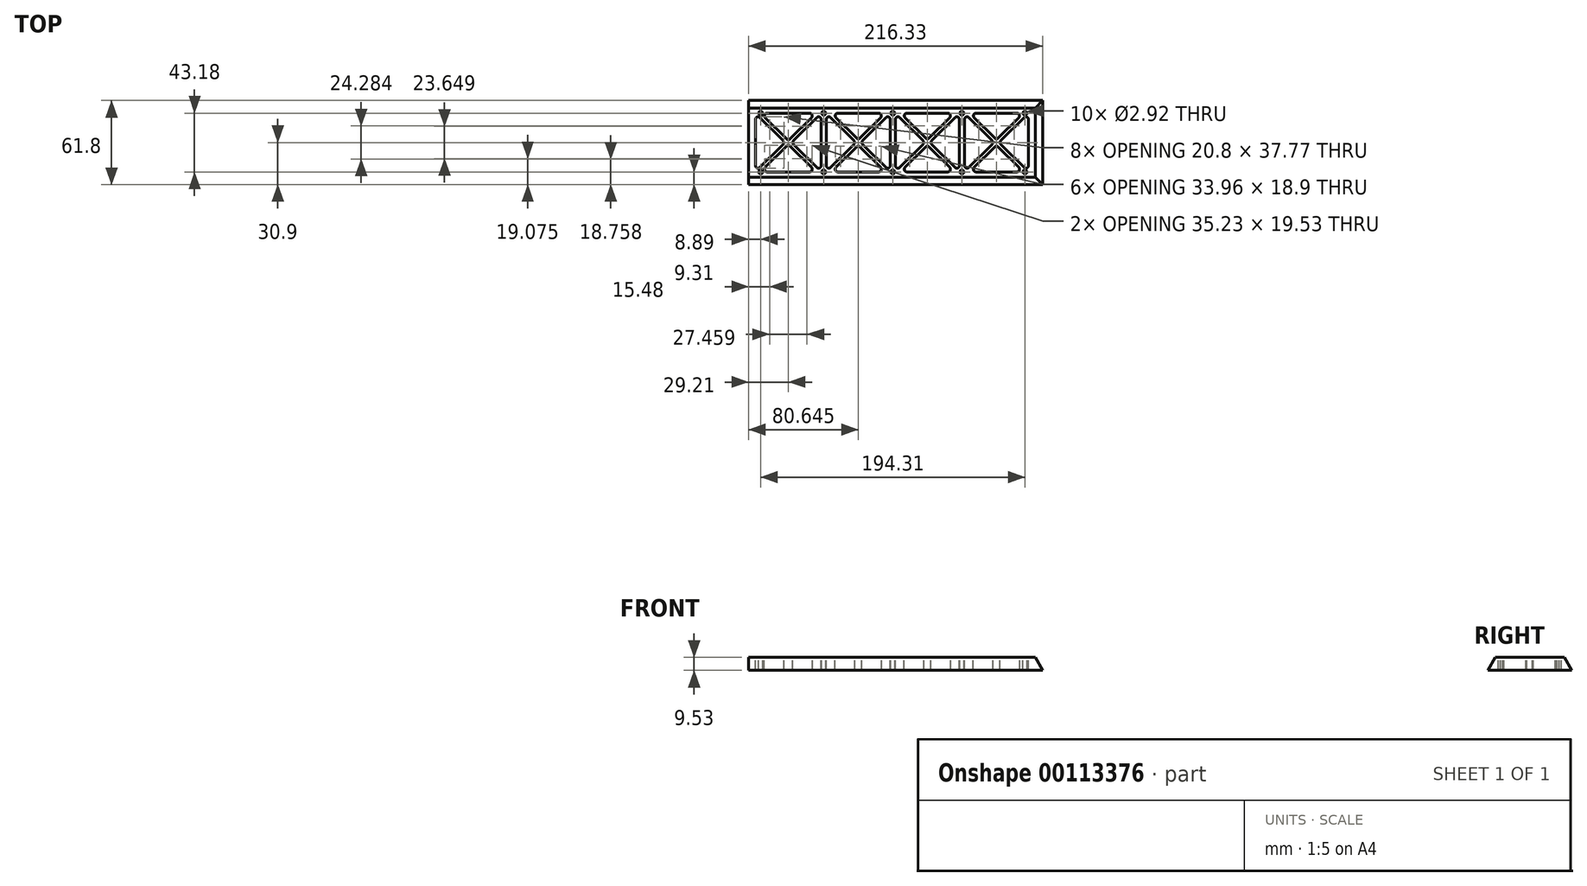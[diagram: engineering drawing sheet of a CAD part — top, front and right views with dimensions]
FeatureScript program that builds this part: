
annotation { "Feature Type Name" : "Feature", "Feature Type Description" : "" }
export const myFeature = defineFeature(function(context is Context, id is Id, definition is map)
    precondition{}
    {
        {
            var Q0;
            Q0=qCreatedBy(makeId("Top.planeOp"),FACE);
            var sketch = newSketch(context, id + "F0", { "sketchPlane" : qUnion([Q0])});
            skLineSegment(sketch, "E0.bottom", {"start": v(0, 0) * mm, "end": v(210.82, 0) * mm});
            skLineSegment(sketch, "E0.top", {"start": v(0, 50.8) * mm, "end": v(210.82, 50.8) * mm});
            skLineSegment(sketch, "E0.left", {"start": v(0, 0) * mm, "end": v(0, 50.8) * mm});
            skLineSegment(sketch, "E0.right", {"start": v(210.82, 0) * mm, "end": v(210.82, 50.8) * mm});
            skSolve(sketch);
        }
        {
            var Q0;
            Q0 = qSketchRegion(id + "F0", true);
            extrude(context, id + "F1", {"entities" : qUnion([Q0]), "depth" : 12.7 * mm, "offsetDistance" : 25.4 * mm});
        }
        {
            var Q0;
            Q0=makeQuery(id+"F1.opExtrude","CAP_FACE",FACE,{"disambiguationData":[OSD([sQuery(id+"F0.wireOp",EDGE,"E0.bottom"),sQuery(id+"F0.wireOp",EDGE,"E0.top"),sQuery(id+"F0.wireOp",EDGE,"E0.left"),sQuery(id+"F0.wireOp",EDGE,"E0.right")])],"isStart":false});
            var sketch = newSketch(context, id + "F2", { "sketchPlane" : qUnion([Q0])});
            skLineSegment(sketch, "E1", {"start": v(0, 25.4) * mm, "end": v(210.82, 25.4) * mm, "construction": true});
            skLineSegment(sketch, "E2", {"start": v(5.08, 42.4) * mm, "end": v(5.08, 8.4) * mm});
            skLineSegment(sketch, "E3", {"start": v(8.33, 7.06) * mm, "end": v(25.32, 24.05) * mm});
            skLineSegment(sketch, "E4", {"start": v(25.32, 26.75) * mm, "end": v(8.33, 43.74) * mm});
            skLineSegment(sketch, "E5", {"start": v(33.1, 26.75) * mm, "end": v(50.09, 43.74) * mm});
            skLineSegment(sketch, "E6", {"start": v(53.34, 42.4) * mm, "end": v(53.34, 8.4) * mm});
            skLineSegment(sketch, "E7", {"start": v(50.09, 7.06) * mm, "end": v(33.1, 24.05) * mm});
            skLineSegment(sketch, "E8", {"start": v(57.15, 42.4) * mm, "end": v(57.15, 8.4) * mm});
            skLineSegment(sketch, "E9", {"start": v(60.4, 7.06) * mm, "end": v(77.4, 24.05) * mm});
            skLineSegment(sketch, "E10", {"start": v(77.4, 26.75) * mm, "end": v(60.4, 43.74) * mm});
            skLineSegment(sketch, "E11", {"start": v(104.14, 42.4) * mm, "end": v(104.14, 8.4) * mm});
            skLineSegment(sketch, "E12", {"start": v(100.89, 7.06) * mm, "end": v(83.9, 24.05) * mm});
            skLineSegment(sketch, "E13", {"start": v(83.9, 26.75) * mm, "end": v(100.89, 43.74) * mm});
            skLineSegment(sketch, "E14", {"start": v(107.95, 42.4) * mm, "end": v(107.95, 8.4) * mm});
            skLineSegment(sketch, "E15", {"start": v(111.2, 7.06) * mm, "end": v(128.2, 24.05) * mm});
            skLineSegment(sketch, "E16", {"start": v(128.2, 26.75) * mm, "end": v(111.2, 43.74) * mm});
            skLineSegment(sketch, "E17", {"start": v(154.94, 42.4) * mm, "end": v(154.94, 8.4) * mm});
            skLineSegment(sketch, "E18", {"start": v(151.69, 7.06) * mm, "end": v(134.7, 24.05) * mm});
            skLineSegment(sketch, "E19", {"start": v(134.7, 26.75) * mm, "end": v(151.69, 43.74) * mm});
            skLineSegment(sketch, "E20", {"start": v(158.75, 42.4) * mm, "end": v(158.75, 8.4) * mm});
            skLineSegment(sketch, "E21", {"start": v(162, 7.06) * mm, "end": v(179, 24.05) * mm});
            skLineSegment(sketch, "E22", {"start": v(179, 26.75) * mm, "end": v(162, 43.74) * mm});
            skLineSegment(sketch, "E23", {"start": v(205.74, 42.4) * mm, "end": v(205.74, 8.4) * mm});
            skLineSegment(sketch, "E24", {"start": v(202.49, 7.06) * mm, "end": v(185.5, 24.05) * mm});
            skLineSegment(sketch, "E25", {"start": v(185.5, 26.75) * mm, "end": v(202.49, 43.74) * mm});
            skLineSegment(sketch, "E26", {"start": v(13.49, 46.99) * mm, "end": v(44.93, 46.99) * mm});
            skLineSegment(sketch, "E27", {"start": v(46.28, 43.74) * mm, "end": v(30.56, 28.02) * mm});
            skLineSegment(sketch, "E28", {"start": v(27.86, 28.02) * mm, "end": v(12.14, 43.74) * mm});
            skLineSegment(sketch, "E29", {"start": v(13.49, 3.8) * mm, "end": v(44.93, 3.8) * mm});
            skLineSegment(sketch, "E30", {"start": v(46.28, 7.06) * mm, "end": v(30.56, 22.78) * mm});
            skLineSegment(sketch, "E31", {"start": v(27.86, 22.78) * mm, "end": v(12.14, 7.06) * mm});
            skLineSegment(sketch, "E32", {"start": v(65.56, 46.99) * mm, "end": v(95.73, 46.99) * mm});
            skLineSegment(sketch, "E33", {"start": v(97.08, 43.74) * mm, "end": v(82, 28.65) * mm});
            skLineSegment(sketch, "E34", {"start": v(79.3, 28.65) * mm, "end": v(64.21, 43.74) * mm});
            skLineSegment(sketch, "E35", {"start": v(65.56, 3.8) * mm, "end": v(95.73, 3.8) * mm});
            skLineSegment(sketch, "E36", {"start": v(97.08, 7.06) * mm, "end": v(82, 22.15) * mm});
            skLineSegment(sketch, "E37", {"start": v(79.3, 22.15) * mm, "end": v(64.21, 7.06) * mm});
            skLineSegment(sketch, "E38", {"start": v(116.36, 46.99) * mm, "end": v(146.53, 46.99) * mm});
            skLineSegment(sketch, "E39", {"start": v(147.88, 43.74) * mm, "end": v(132.8, 28.65) * mm});
            skLineSegment(sketch, "E40", {"start": v(130.1, 28.65) * mm, "end": v(115.01, 43.74) * mm});
            skLineSegment(sketch, "E41", {"start": v(116.36, 3.8) * mm, "end": v(146.53, 3.8) * mm});
            skLineSegment(sketch, "E42", {"start": v(147.88, 7.06) * mm, "end": v(132.8, 22.15) * mm});
            skLineSegment(sketch, "E43", {"start": v(130.1, 22.15) * mm, "end": v(115.01, 7.06) * mm});
            skLineSegment(sketch, "E44", {"start": v(167.16, 46.99) * mm, "end": v(197.33, 46.99) * mm});
            skLineSegment(sketch, "E45", {"start": v(198.68, 43.74) * mm, "end": v(183.6, 28.65) * mm});
            skLineSegment(sketch, "E46", {"start": v(180.9, 28.65) * mm, "end": v(165.81, 43.74) * mm});
            skLineSegment(sketch, "E47", {"start": v(167.16, 3.8) * mm, "end": v(197.33, 3.8) * mm});
            skLineSegment(sketch, "E48", {"start": v(198.68, 7.06) * mm, "end": v(183.6, 22.15) * mm});
            skLineSegment(sketch, "E49", {"start": v(180.9, 22.15) * mm, "end": v(165.81, 7.06) * mm});
            skPoint(sketch, "E50.visualSharp", {"position": v(5.08, 46.99) * mm});
            skArc(sketch, "E50.filletArc", {"start": v(8.33, 43.74) * mm, "mid": v(6.26, 44.15) * mm, "end": v(5.08, 42.4) * mm});
            skPoint(sketch, "E51.visualSharp", {"position": v(5.08, 3.8) * mm});
            skArc(sketch, "E51.filletArc", {"start": v(5.08, 8.4) * mm, "mid": v(6.26, 6.65) * mm, "end": v(8.33, 7.06) * mm});
            skPoint(sketch, "E52.visualSharp", {"position": v(26.67, 25.4) * mm});
            skArc(sketch, "E52.filletArc", {"start": v(25.32, 24.05) * mm, "mid": v(25.88, 25.4) * mm, "end": v(25.32, 26.75) * mm});
            skPoint(sketch, "E53.visualSharp", {"position": v(8.89, 46.99) * mm});
            skArc(sketch, "E53.filletArc", {"start": v(13.49, 46.99) * mm, "mid": v(11.73, 45.81) * mm, "end": v(12.14, 43.74) * mm});
            skPoint(sketch, "E54.visualSharp", {"position": v(49.53, 46.99) * mm});
            skArc(sketch, "E54.filletArc", {"start": v(46.28, 43.74) * mm, "mid": v(46.7, 45.81) * mm, "end": v(44.93, 46.99) * mm});
            skPoint(sketch, "E55.visualSharp", {"position": v(29.21, 26.67) * mm});
            skArc(sketch, "E55.filletArc", {"start": v(27.86, 28.02) * mm, "mid": v(29.21, 27.46) * mm, "end": v(30.56, 28.02) * mm});
            skPoint(sketch, "E56.visualSharp", {"position": v(29.21, 24.13) * mm});
            skArc(sketch, "E56.filletArc", {"start": v(30.56, 22.78) * mm, "mid": v(29.21, 23.34) * mm, "end": v(27.86, 22.78) * mm});
            skPoint(sketch, "E57.visualSharp", {"position": v(8.9, 3.8) * mm});
            skArc(sketch, "E57.filletArc", {"start": v(12.14, 7.06) * mm, "mid": v(11.73, 4.99) * mm, "end": v(13.49, 3.8) * mm});
            skPoint(sketch, "E58.visualSharp", {"position": v(49.53, 3.8) * mm});
            skArc(sketch, "E58.filletArc", {"start": v(44.93, 3.8) * mm, "mid": v(46.7, 4.99) * mm, "end": v(46.28, 7.06) * mm});
            skPoint(sketch, "E59.visualSharp", {"position": v(31.75, 25.4) * mm});
            skArc(sketch, "E59.filletArc", {"start": v(33.1, 26.75) * mm, "mid": v(32.54, 25.4) * mm, "end": v(33.1, 24.05) * mm});
            skPoint(sketch, "E60.visualSharp", {"position": v(53.34, 46.99) * mm});
            skArc(sketch, "E60.filletArc", {"start": v(53.34, 42.4) * mm, "mid": v(52.16, 44.15) * mm, "end": v(50.09, 43.74) * mm});
            skPoint(sketch, "E61.visualSharp", {"position": v(53.34, 3.8) * mm});
            skArc(sketch, "E61.filletArc", {"start": v(50.09, 7.06) * mm, "mid": v(52.16, 6.65) * mm, "end": v(53.34, 8.4) * mm});
            skPoint(sketch, "E62.visualSharp", {"position": v(57.15, 46.99) * mm});
            skArc(sketch, "E62.filletArc", {"start": v(60.4, 43.74) * mm, "mid": v(58.33, 44.15) * mm, "end": v(57.15, 42.4) * mm});
            skPoint(sketch, "E63.visualSharp", {"position": v(57.15, 3.8) * mm});
            skArc(sketch, "E63.filletArc", {"start": v(57.15, 8.4) * mm, "mid": v(58.33, 6.65) * mm, "end": v(60.4, 7.06) * mm});
            skPoint(sketch, "E64.visualSharp", {"position": v(78.74, 25.4) * mm});
            skArc(sketch, "E64.filletArc", {"start": v(77.4, 24.05) * mm, "mid": v(77.95, 25.4) * mm, "end": v(77.4, 26.75) * mm});
            skPoint(sketch, "E65.visualSharp", {"position": v(60.96, 46.99) * mm});
            skArc(sketch, "E65.filletArc", {"start": v(65.56, 46.99) * mm, "mid": v(63.8, 45.81) * mm, "end": v(64.21, 43.74) * mm});
            skPoint(sketch, "E66.visualSharp", {"position": v(100.33, 46.99) * mm});
            skArc(sketch, "E66.filletArc", {"start": v(97.08, 43.74) * mm, "mid": v(97.5, 45.81) * mm, "end": v(95.73, 46.99) * mm});
            skPoint(sketch, "E67.visualSharp", {"position": v(80.64, 27.3) * mm});
            skArc(sketch, "E67.filletArc", {"start": v(79.3, 28.65) * mm, "mid": v(80.65, 28.1) * mm, "end": v(82, 28.65) * mm});
            skPoint(sketch, "E68.visualSharp", {"position": v(80.64, 23.5) * mm});
            skArc(sketch, "E68.filletArc", {"start": v(82, 22.15) * mm, "mid": v(80.65, 22.7) * mm, "end": v(79.3, 22.15) * mm});
            skPoint(sketch, "E69.visualSharp", {"position": v(60.96, 3.8) * mm});
            skArc(sketch, "E69.filletArc", {"start": v(64.21, 7.06) * mm, "mid": v(63.8, 4.99) * mm, "end": v(65.56, 3.8) * mm});
            skPoint(sketch, "E70.visualSharp", {"position": v(100.33, 3.8) * mm});
            skArc(sketch, "E70.filletArc", {"start": v(95.73, 3.8) * mm, "mid": v(97.5, 4.99) * mm, "end": v(97.08, 7.06) * mm});
            skPoint(sketch, "E71.visualSharp", {"position": v(82.55, 25.4) * mm});
            skArc(sketch, "E71.filletArc", {"start": v(83.9, 26.75) * mm, "mid": v(83.34, 25.4) * mm, "end": v(83.9, 24.05) * mm});
            skPoint(sketch, "E72.visualSharp", {"position": v(104.14, 46.99) * mm});
            skArc(sketch, "E72.filletArc", {"start": v(104.14, 42.4) * mm, "mid": v(102.96, 44.15) * mm, "end": v(100.89, 43.74) * mm});
            skPoint(sketch, "E73.visualSharp", {"position": v(104.14, 3.8) * mm});
            skArc(sketch, "E73.filletArc", {"start": v(100.89, 7.06) * mm, "mid": v(102.96, 6.65) * mm, "end": v(104.14, 8.4) * mm});
            skPoint(sketch, "E74.visualSharp", {"position": v(107.95, 46.99) * mm});
            skArc(sketch, "E74.filletArc", {"start": v(111.2, 43.74) * mm, "mid": v(109.13, 44.15) * mm, "end": v(107.95, 42.4) * mm});
            skPoint(sketch, "E75.visualSharp", {"position": v(129.54, 25.4) * mm});
            skArc(sketch, "E75.filletArc", {"start": v(128.2, 24.05) * mm, "mid": v(128.75, 25.4) * mm, "end": v(128.2, 26.75) * mm});
            skPoint(sketch, "E76.visualSharp", {"position": v(107.95, 3.8) * mm});
            skArc(sketch, "E76.filletArc", {"start": v(107.95, 8.4) * mm, "mid": v(109.13, 6.65) * mm, "end": v(111.2, 7.06) * mm});
            skPoint(sketch, "E77.visualSharp", {"position": v(111.76, 46.99) * mm});
            skArc(sketch, "E77.filletArc", {"start": v(116.36, 46.99) * mm, "mid": v(114.6, 45.81) * mm, "end": v(115.01, 43.74) * mm});
            skPoint(sketch, "E78.visualSharp", {"position": v(151.13, 46.99) * mm});
            skArc(sketch, "E78.filletArc", {"start": v(147.88, 43.74) * mm, "mid": v(148.3, 45.81) * mm, "end": v(146.53, 46.99) * mm});
            skPoint(sketch, "E79.visualSharp", {"position": v(131.44, 27.3) * mm});
            skArc(sketch, "E79.filletArc", {"start": v(130.1, 28.65) * mm, "mid": v(131.44, 28.1) * mm, "end": v(132.8, 28.65) * mm});
            skPoint(sketch, "E80.visualSharp", {"position": v(133.35, 25.4) * mm});
            skArc(sketch, "E80.filletArc", {"start": v(134.7, 26.75) * mm, "mid": v(134.14, 25.4) * mm, "end": v(134.7, 24.05) * mm});
            skPoint(sketch, "E81.visualSharp", {"position": v(154.94, 46.99) * mm});
            skArc(sketch, "E81.filletArc", {"start": v(154.94, 42.4) * mm, "mid": v(153.76, 44.15) * mm, "end": v(151.69, 43.74) * mm});
            skPoint(sketch, "E82.visualSharp", {"position": v(154.94, 3.8) * mm});
            skArc(sketch, "E82.filletArc", {"start": v(151.69, 7.06) * mm, "mid": v(153.76, 6.65) * mm, "end": v(154.94, 8.4) * mm});
            skPoint(sketch, "E83.visualSharp", {"position": v(131.44, 23.5) * mm});
            skArc(sketch, "E83.filletArc", {"start": v(132.8, 22.15) * mm, "mid": v(131.44, 22.7) * mm, "end": v(130.1, 22.15) * mm});
            skPoint(sketch, "E84.visualSharp", {"position": v(111.76, 3.8) * mm});
            skArc(sketch, "E84.filletArc", {"start": v(115.01, 7.06) * mm, "mid": v(114.6, 4.99) * mm, "end": v(116.36, 3.8) * mm});
            skPoint(sketch, "E85.visualSharp", {"position": v(151.13, 3.8) * mm});
            skArc(sketch, "E85.filletArc", {"start": v(146.53, 3.8) * mm, "mid": v(148.3, 4.99) * mm, "end": v(147.88, 7.06) * mm});
            skPoint(sketch, "E86.visualSharp", {"position": v(158.75, 46.99) * mm});
            skArc(sketch, "E86.filletArc", {"start": v(162, 43.74) * mm, "mid": v(159.93, 44.15) * mm, "end": v(158.75, 42.4) * mm});
            skPoint(sketch, "E87.visualSharp", {"position": v(158.75, 3.8) * mm});
            skArc(sketch, "E87.filletArc", {"start": v(158.75, 8.4) * mm, "mid": v(159.93, 6.65) * mm, "end": v(162, 7.06) * mm});
            skPoint(sketch, "E88.visualSharp", {"position": v(180.34, 25.4) * mm});
            skArc(sketch, "E88.filletArc", {"start": v(179, 24.05) * mm, "mid": v(179.55, 25.4) * mm, "end": v(179, 26.75) * mm});
            skPoint(sketch, "E89.visualSharp", {"position": v(162.56, 3.8) * mm});
            skArc(sketch, "E89.filletArc", {"start": v(165.81, 7.06) * mm, "mid": v(165.4, 4.99) * mm, "end": v(167.16, 3.8) * mm});
            skPoint(sketch, "E90.visualSharp", {"position": v(182.24, 23.5) * mm});
            skArc(sketch, "E90.filletArc", {"start": v(183.6, 22.15) * mm, "mid": v(182.24, 22.7) * mm, "end": v(180.9, 22.15) * mm});
            skPoint(sketch, "E91.visualSharp", {"position": v(201.93, 3.8) * mm});
            skArc(sketch, "E91.filletArc", {"start": v(197.33, 3.8) * mm, "mid": v(199.1, 4.99) * mm, "end": v(198.68, 7.06) * mm});
            skPoint(sketch, "E92.visualSharp", {"position": v(162.56, 46.99) * mm});
            skArc(sketch, "E92.filletArc", {"start": v(167.16, 46.99) * mm, "mid": v(165.4, 45.81) * mm, "end": v(165.81, 43.74) * mm});
            skPoint(sketch, "E93.visualSharp", {"position": v(201.93, 46.99) * mm});
            skArc(sketch, "E93.filletArc", {"start": v(198.68, 43.74) * mm, "mid": v(199.1, 45.81) * mm, "end": v(197.33, 46.99) * mm});
            skPoint(sketch, "E94.visualSharp", {"position": v(182.24, 27.3) * mm});
            skArc(sketch, "E94.filletArc", {"start": v(180.9, 28.65) * mm, "mid": v(182.24, 28.1) * mm, "end": v(183.6, 28.65) * mm});
            skPoint(sketch, "E95.visualSharp", {"position": v(184.15, 25.4) * mm});
            skArc(sketch, "E95.filletArc", {"start": v(185.5, 26.75) * mm, "mid": v(184.94, 25.4) * mm, "end": v(185.5, 24.05) * mm});
            skPoint(sketch, "E96.visualSharp", {"position": v(205.74, 46.99) * mm});
            skArc(sketch, "E96.filletArc", {"start": v(205.74, 42.4) * mm, "mid": v(204.56, 44.15) * mm, "end": v(202.49, 43.74) * mm});
            skPoint(sketch, "E97.visualSharp", {"position": v(205.74, 3.8) * mm});
            skArc(sketch, "E97.filletArc", {"start": v(202.49, 7.06) * mm, "mid": v(204.56, 6.65) * mm, "end": v(205.74, 8.4) * mm});
            skSolve(sketch);
        }
        {
            var Q0;
            Q0 = qSketchRegion(id + "F2", true);
            extrude(context, id + "F3", {"entities" : qUnion([Q0]), "operationType" : NewBodyOperationType.REMOVE, "oppositeDirection" : true, "depth" : 10.16 * mm, "offsetDistance" : 25.4 * mm});
        }
        {
            var Q0;
            Q0=makeQuery(id+"F1.opExtrude","CAP_FACE",FACE,{"disambiguationData":[OSD([sQuery(id+"F0.wireOp",EDGE,"E0.bottom"),sQuery(id+"F0.wireOp",EDGE,"E0.top"),sQuery(id+"F0.wireOp",EDGE,"E0.left"),sQuery(id+"F0.wireOp",EDGE,"E0.right")])],"isStart":true});
            extrude(context, id + "F4", {"entities" : qUnion([Q0]), "operationType" : NewBodyOperationType.REMOVE, "oppositeDirection" : true, "depth" : 3.17 * mm, "offsetDistance" : 25.4 * mm});
        }
        {
            var Q0;
            Q0=makeQuery(id+"F1.opExtrude","SWEPT_FACE",FACE,{"disambiguationData":[OSD([sQuery(id+"F0.wireOp",EDGE,"E0.left")])]});
            var sketch = newSketch(context, id + "F5", { "sketchPlane" : qUnion([Q0])});
            skLineSegment(sketch, "E98", {"start": v(-50.8, 3.18) * mm, "end": v(-56.3, 3.18) * mm});
            skLineSegment(sketch, "E99", {"start": v(-56.3, 3.18) * mm, "end": v(-50.8, 12.7) * mm});
            skLineSegment(sketch, "E100", {"start": v(-50.8, 12.7) * mm, "end": v(-50.8, 3.18) * mm});
            skLineSegment(sketch, "E101", {"start": v(0, 3.18) * mm, "end": v(5.5, 3.18) * mm});
            skLineSegment(sketch, "E102", {"start": v(5.5, 3.17) * mm, "end": v(0, 12.7) * mm});
            skLineSegment(sketch, "E103", {"start": v(0, 12.7) * mm, "end": v(0, 3.18) * mm});
            skSolve(sketch);
        }
        {
            var Q0;
            Q0 = qSketchRegion(id + "F5", true);
            extrude(context, id + "F6", {"entities" : qUnion([Q0]), "operationType" : NewBodyOperationType.ADD, "oppositeDirection" : true, "depth" : 210.82 * mm, "offsetDistance" : 25.4 * mm});
        }
        {
            var Q0;
            Q0=makeQuery(id+"F6.boolean.opBoolean","MERGE",FACE,{"derivedFrom":[makeQuery(id+"F1.opExtrude","SWEPT_FACE",FACE,{"disambiguationData":[OSD([sQuery(id+"F0.wireOp",EDGE,"E0.right")])]}),makeQuery(id+"F6.opExtrude","CAP_FACE",FACE,{"disambiguationData":[OSD([sQuery(id+"F5.wireOp",EDGE,"E98"),sQuery(id+"F5.wireOp",EDGE,"E99"),sQuery(id+"F5.wireOp",EDGE,"E100")])],"isStart":false}),makeQuery(id+"F6.opExtrude","CAP_FACE",FACE,{"disambiguationData":[OSD([sQuery(id+"F5.wireOp",EDGE,"E101"),sQuery(id+"F5.wireOp",EDGE,"E102"),sQuery(id+"F5.wireOp",EDGE,"E103")])],"isStart":false})]});
            extrude(context, id + "F7", {"entities" : qUnion([Q0]), "operationType" : NewBodyOperationType.ADD, "depth" : 5.5 * mm, "offsetDistance" : 25.4 * mm});
        }
        {
            var Q0;
            Q0=makeQuery(id+"F7.opExtrude","CAP_EDGE",EDGE,{"disambiguationData":[OSD([sQuery(id+"F0.wireOp",EDGE,"E0.right")])],"isStart":false});
            chamfer(context, id + "F8", {"entities" : qUnion([Q0]), "chamferType" : ChamferType.OFFSET_ANGLE, "width" : 9.52 * mm, "oppositeDirection" : true, "angle" : 30 * degree, "tangentPropagation" : true});
        }
        {
            var Q0;
            {var subQ0=sQuery(id+"F0.wireOp",EDGE,"E0.right");Q0=makeQuery(id+"F7.boolean.opBoolean","MERGE",FACE,{"derivedFrom":[makeQuery(id+"F1.opExtrude","CAP_FACE",FACE,{"disambiguationData":[OSD([sQuery(id+"F0.wireOp",EDGE,"E0.bottom"),sQuery(id+"F0.wireOp",EDGE,"E0.top"),sQuery(id+"F0.wireOp",EDGE,"E0.left"),subQ0])],"isStart":false}),makeQuery(id+"F7.opExtrude","SWEPT_FACE",FACE,{"disambiguationData":[OSD([subQ0])]})]});}
            var sketch = newSketch(context, id + "F9", { "sketchPlane" : qUnion([Q0])});
            skCircle(sketch, "E104", {"center": v(8.9, 47) * mm, "radius": 1.46 * mm});
            skCircle(sketch, "E105", {"center": v(8.9, 3.8) * mm, "radius": 1.46 * mm});
            skCircle(sketch, "E106", {"center": v(55.25, 47) * mm, "radius": 1.46 * mm});
            skCircle(sketch, "E107", {"center": v(55.25, 3.8) * mm, "radius": 1.46 * mm});
            skCircle(sketch, "E108", {"center": v(106.05, 47) * mm, "radius": 1.46 * mm});
            skCircle(sketch, "E109", {"center": v(106.05, 3.81) * mm, "radius": 1.46 * mm});
            skCircle(sketch, "E110", {"center": v(156.84, 47) * mm, "radius": 1.46 * mm});
            skCircle(sketch, "E111", {"center": v(156.84, 3.81) * mm, "radius": 1.46 * mm});
            skCircle(sketch, "E112", {"center": v(203.2, 47) * mm, "radius": 1.46 * mm});
            skCircle(sketch, "E113", {"center": v(203.2, 3.81) * mm, "radius": 1.46 * mm});
            skSolve(sketch);
        }
        {
            var Q0;
            Q0 = qSketchRegion(id + "F9", true);
            extrude(context, id + "F10", {"entities" : qUnion([Q0]), "operationType" : NewBodyOperationType.REMOVE, "oppositeDirection" : true, "depth" : 9.52 * mm, "offsetDistance" : 25.4 * mm});
        }
    });
